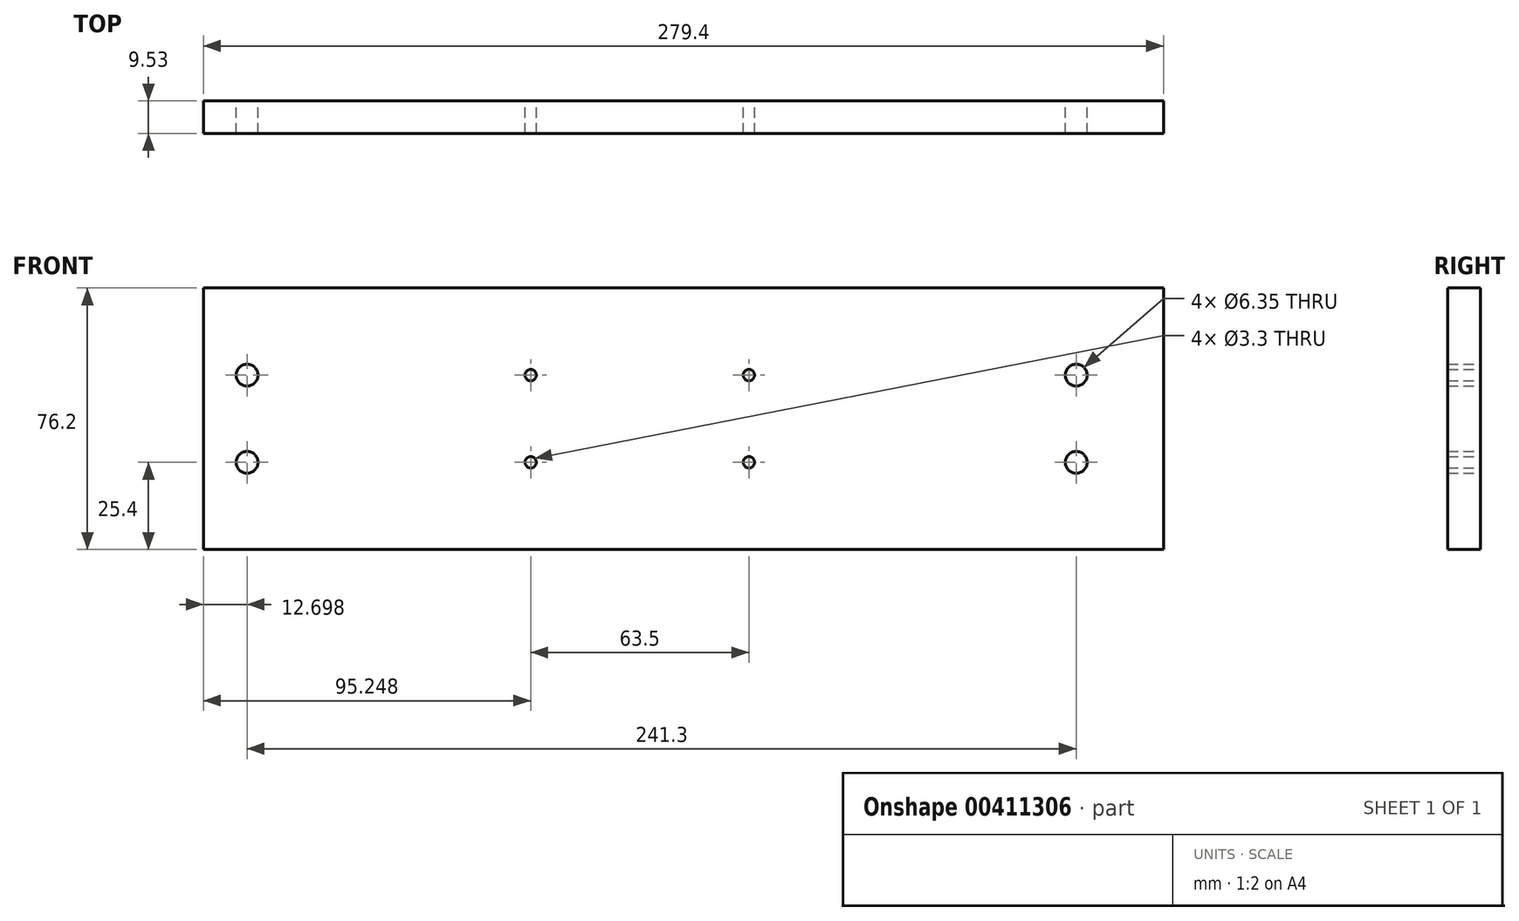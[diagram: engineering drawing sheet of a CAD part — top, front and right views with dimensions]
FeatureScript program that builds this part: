
annotation { "Feature Type Name" : "Feature", "Feature Type Description" : "" }
export const myFeature = defineFeature(function(context is Context, id is Id, definition is map)
    precondition{}
    {
        {
            var Q0;
            Q0=qCreatedBy(makeId("Front.planeOp"),FACE);
            var sketch = newSketch(context, id + "F0", { "sketchPlane" : qUnion([Q0])});
            skLineSegment(sketch, "E0.bottom", {"start": v(-137.87, 38.1) * mm, "end": v(141.53, 38.1) * mm});
            skLineSegment(sketch, "E0.top", {"start": v(-137.87, -38.1) * mm, "end": v(141.53, -38.1) * mm});
            skLineSegment(sketch, "E0.left", {"start": v(-137.87, 38.1) * mm, "end": v(-137.87, -38.1) * mm});
            skLineSegment(sketch, "E0.right", {"start": v(141.53, 38.1) * mm, "end": v(141.53, -38.1) * mm});
            skCircle(sketch, "E1", {"center": v(-125.17, 12.7) * mm, "radius": 3.18 * mm});
            skCircle(sketch, "E2", {"center": v(-42.62, 12.7) * mm, "radius": 1.65 * mm});
            skCircle(sketch, "E3", {"center": v(20.88, 12.7) * mm, "radius": 1.65 * mm});
            skCircle(sketch, "E4", {"center": v(116.13, 12.7) * mm, "radius": 3.18 * mm});
            skCircle(sketch, "E5", {"center": v(-125.17, -12.7) * mm, "radius": 3.18 * mm});
            skCircle(sketch, "E6", {"center": v(-42.62, -12.7) * mm, "radius": 1.65 * mm});
            skCircle(sketch, "E7", {"center": v(20.88, -12.7) * mm, "radius": 1.65 * mm});
            skCircle(sketch, "E8", {"center": v(116.13, -12.7) * mm, "radius": 3.18 * mm});
            skSolve(sketch);
        }
        {
            var Q0;
            Q0=makeQuery(id+"F0.imprint","IMPRINT",FACE,{"disambiguationData":[TD([[makeQuery(id+"F0.imprint","IMPRINT",EDGE,{"derivedFrom":sQuery(id+"F0.wireOp",EDGE,"E0.bottom")}),-1.0]])]});
            extrude(context, id + "F1", {"entities" : qUnion([Q0]), "depth" : 9.52 * mm});
        }
    });
